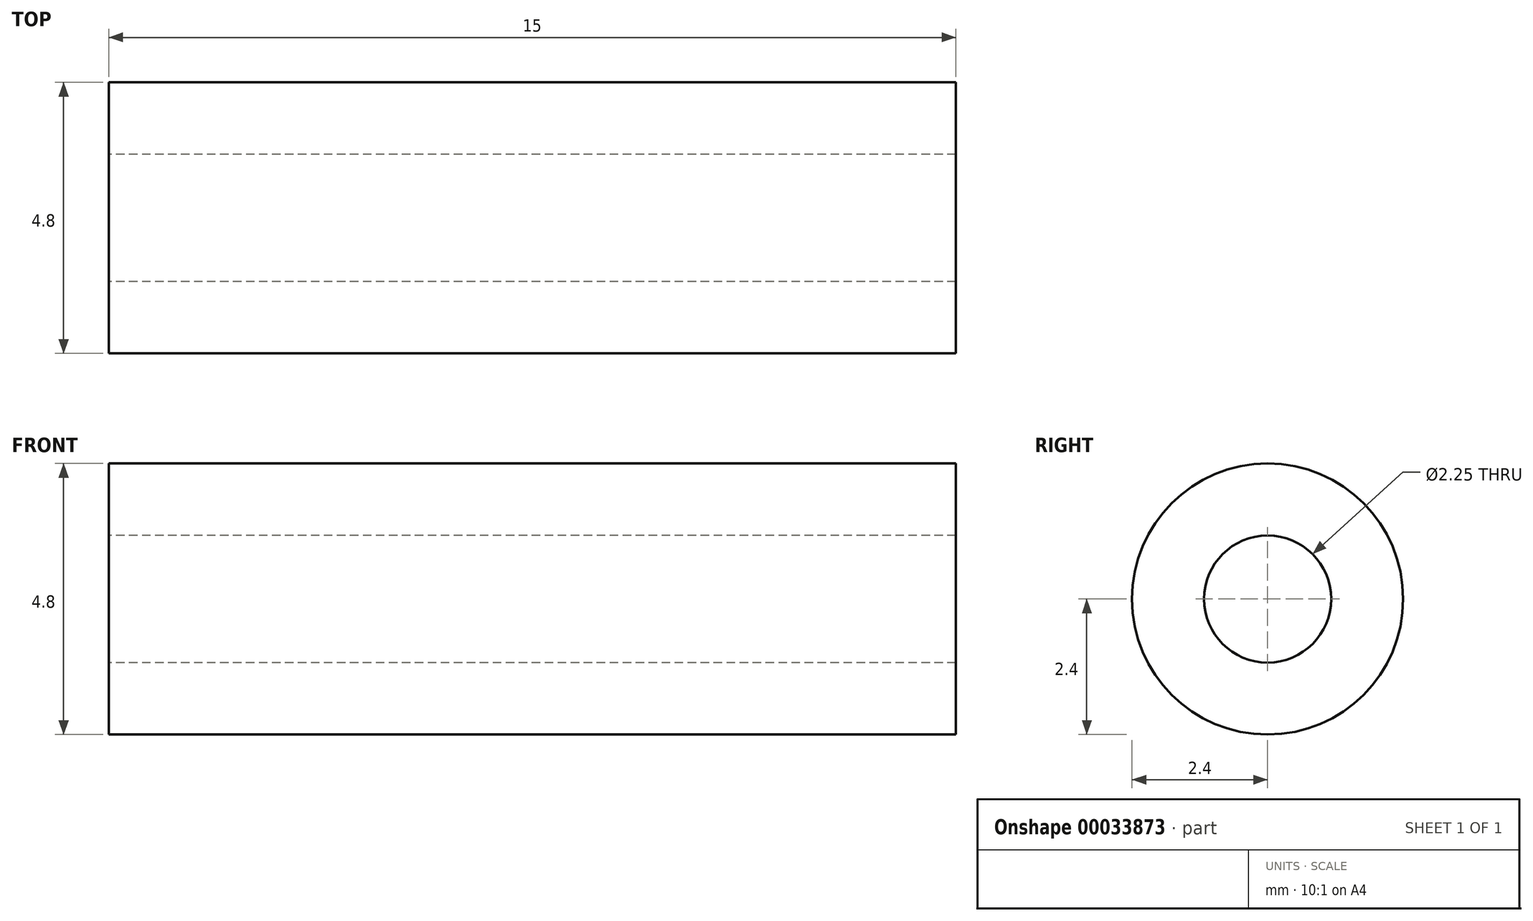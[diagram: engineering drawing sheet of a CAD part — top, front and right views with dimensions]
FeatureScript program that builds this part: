
annotation { "Feature Type Name" : "Feature", "Feature Type Description" : "" }
export const myFeature = defineFeature(function(context is Context, id is Id, definition is map)
    precondition{}
    {
        {
            var Q0;
            Q0=qCreatedBy(makeId("Right.planeOp"),FACE);
            var sketch = newSketch(context, id + "F0", { "sketchPlane" : qUnion([Q0])});
            skCircle(sketch, "E0", {"center": v(0, 0) * mm, "radius": 2.4 * mm});
            skCircle(sketch, "E1", {"center": v(0, 0) * mm, "radius": 1.13 * mm});
            skSolve(sketch);
        }
        {
            var Q0;
            Q0 = qSketchRegion(id + "F0", true);
            extrude(context, id + "F1", {"entities" : qUnion([Q0]), "depth" : 15 * mm});
        }
    });
